# Revit family: HBLC
name_source: partatom
category: Lighting Fixtures
revit_build: Autodesk Revit 2014 (Build: 20130308_1515(x64)
units: mm (PartAtom-declared; Revit-internal decimal feet)

## types (1)
- HBLC
    Apparent Load = 188 VA
    Certification = CSA Listed to UL844
• CSA Listed to UL1598 Wet Location
• Wet Location listed up to 90 degrees
• Damp location listed at greater than 90 degrees mounting angle
• Class I, Division 2, Groups A, B, C & D
• IP66 with factory installed ENCG option
    Color Filter = 16777215
    Default Elevation = 48 "
    Description = The HBLC LED High Bay is specifically designed to be used on heavy industrial bridge cranes while utilizing AC or DC input voltage. Custom engineered LED optics provide evenly distributed light for bridge crane operators and others working under the crane for increased visibility and safety.
    Dimming Lamp Color Temperature Shift = <None>
    Emit Shape Visible in Rendering = No
    Emit from Circle Diameter = 11 "
    Environmental Conditions = Damp Location, Wet Location, outdoor
    Fastners = Paint - Hubbell - Light Silver
    Features = LED source is resistant to vibration
Lights area below bridge crane
Yoke mount for strength and mounting flexibility
Hinged housing is easy to service
Rugged die-cast construction
Sealed, wet location rated design
Vibration tested at 3G
The HBLC is suitable for bridge cranes and other high vibration industrial areas.
    Glass = Hubbell - Glass
    IP Rating = IP56
    Lamp = LED
    Load Classification = Lighting
    Manufacturer = Hubbell Industrial Lighting
    Material Finish = Paint - Hubbell - White Texture
    Model = HBLC
    Optics = Narrow
    Photometric Web File = Generic.ies
    Power Factor = 0.9
    Product Documentation Link = https://hubbellcdn.com
    Product Page URL = https://www.hubbell.com
    Tilt Angle = -90.00°
    URL = http://www.hubbellindustrial.com
    Voltage = 120 V
    Warranty = Five years from date of purchase when used on supply AC power
• One year from date of purchase when used on supply DC power
    Watt = 169 W
    Wattage Comments = 169W

## geometry (parser evidence)
native form markers: Blend x2, Sweep x5
no freeform markers — native parametric forms only
